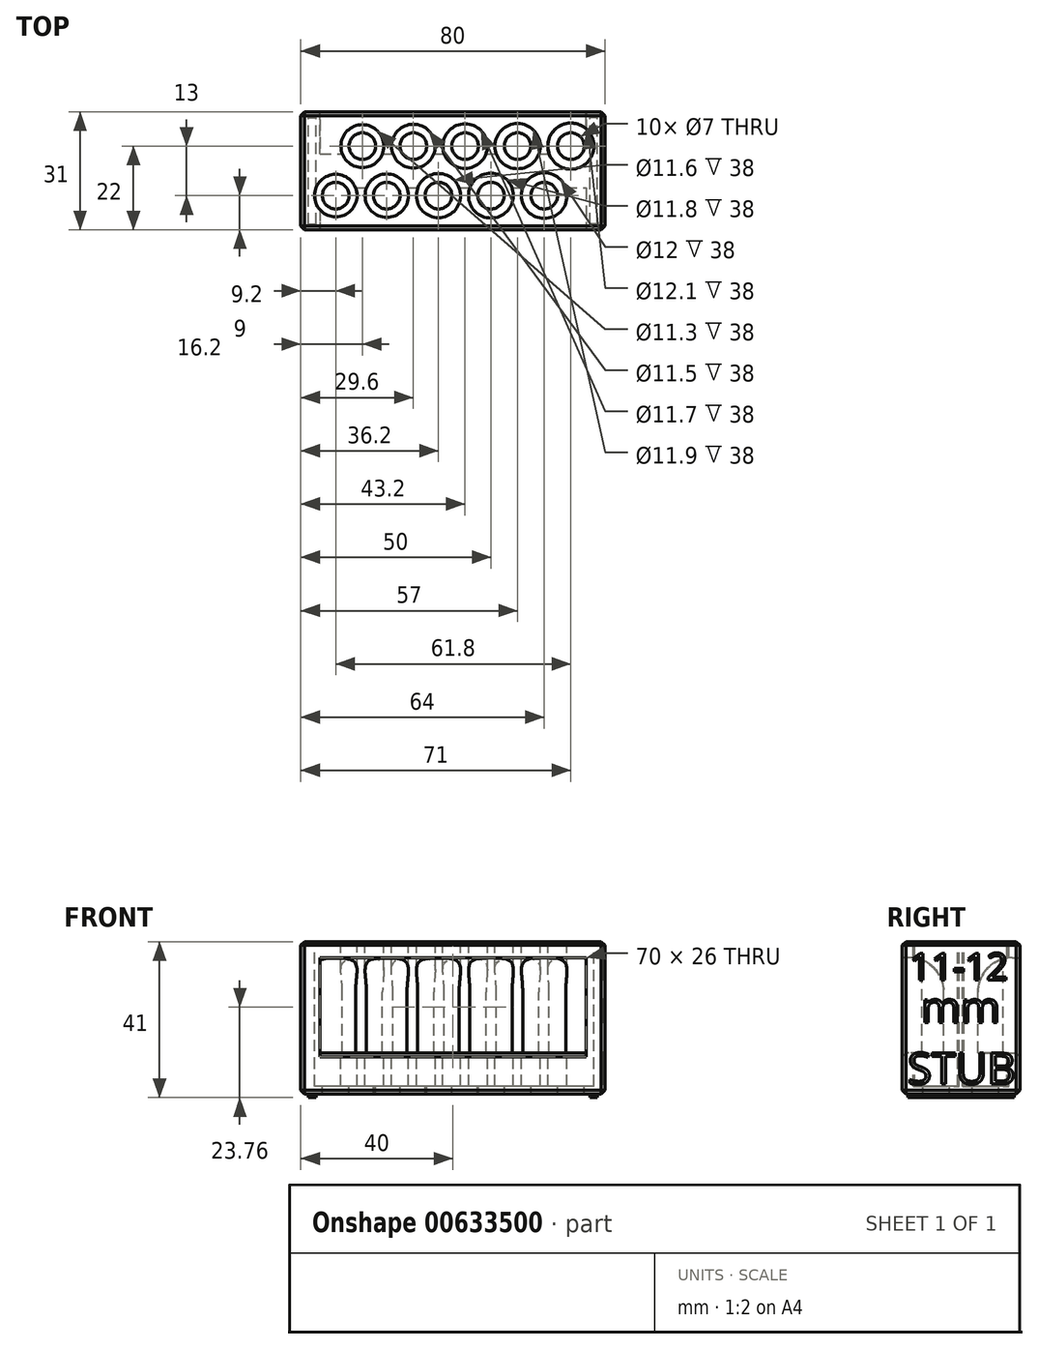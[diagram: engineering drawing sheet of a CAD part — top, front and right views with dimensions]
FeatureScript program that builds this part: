
annotation { "Feature Type Name" : "Feature", "Feature Type Description" : "" }
export const myFeature = defineFeature(function(context is Context, id is Id, definition is map)
    precondition{}
    {
        {
            var Q0;
            Q0=qCreatedBy(makeId("Top.planeOp"),FACE);
            var sketch = newSketch(context, id + "F0", { "sketchPlane" : qUnion([Q0])});
            skCircle(sketch, "E0", {"center": v(0, 0) * mm, "radius": 6.05 * mm});
            skCircle(sketch, "E1.1.0.0", {"center": v(-14, 0) * mm, "radius": 5.95 * mm});
            skCircle(sketch, "E1.2.0.0", {"center": v(-27.8, 0) * mm, "radius": 5.85 * mm});
            skCircle(sketch, "E1.3.0.0", {"center": v(-41.4, 0) * mm, "radius": 5.75 * mm});
            skCircle(sketch, "E1.4.0.0", {"center": v(-54.8, 0) * mm, "radius": 5.65 * mm});
            skLineSegment(sketch, "E1.direction1", {"start": v(0, 0) * mm, "end": v(-14, 0) * mm, "construction": true});
            skLineSegment(sketch, "E2", {"start": v(0, 0) * mm, "end": v(0, -13) * mm, "construction": true});
            skLineSegment(sketch, "E3", {"start": v(0, -13) * mm, "end": v(-90, -13) * mm, "construction": true});
            skCircle(sketch, "E4", {"center": v(-7, -13) * mm, "radius": 6 * mm});
            skCircle(sketch, "E5.1.0.0", {"center": v(-21, -13) * mm, "radius": 5.9 * mm});
            skCircle(sketch, "E5.2.0.0", {"center": v(-34.8, -13) * mm, "radius": 5.8 * mm});
            skCircle(sketch, "E5.3.0.0", {"center": v(-48.4, -13) * mm, "radius": 5.7 * mm});
            skCircle(sketch, "E5.4.0.0", {"center": v(-61.8, -13) * mm, "radius": 5.6 * mm});
            skLineSegment(sketch, "E5.direction1", {"start": v(-7, -13) * mm, "end": v(-21, -13) * mm, "construction": true});
            skSolve(sketch);
        }
        {
            var Q0;
            Q0=qCreatedBy(makeId("Top.planeOp"),FACE);
            var sketch = newSketch(context, id + "F1", { "sketchPlane" : qUnion([Q0])});
            skLineSegment(sketch, "E6.bottom", {"start": v(9, 9) * mm, "end": v(-71, 9) * mm});
            skLineSegment(sketch, "E6.top", {"start": v(9, -22) * mm, "end": v(-71, -22) * mm});
            skLineSegment(sketch, "E6.left", {"start": v(9, 9) * mm, "end": v(9, -22) * mm});
            skLineSegment(sketch, "E6.right", {"start": v(-71, 9) * mm, "end": v(-71, -22) * mm});
            skSolve(sketch);
        }
        {
            var Q0;
            Q0=makeQuery(id+"F1.imprint","IMPRINT",FACE,{"disambiguationData":[TD([[makeQuery(id+"F1.imprint","IMPRINT",EDGE,{"derivedFrom":sQuery(id+"F1.wireOp",EDGE,"E6.bottom")}),1.0]])]});
            extrude(context, id + "F2", {"entities" : qUnion([Q0]), "oppositeDirection" : true, "depth" : 40 * mm, "offsetDistance" : 25 * mm});
        }
        {
            var Q0;
            Q0 = qSketchRegion(id + "F0", true);
            extrude(context, id + "F3", {"entities" : qUnion([Q0]), "operationType" : NewBodyOperationType.REMOVE, "oppositeDirection" : true, "depth" : 38 * mm, "offsetDistance" : 25 * mm});
        }
        {
            var Q0;
            Q0=qCreatedBy(makeId("Top.planeOp"),FACE);
            var sketch = newSketch(context, id + "F4", { "sketchPlane" : qUnion([Q0])});
            skLineSegment(sketch, "E7.direction1", {"start": v(0, 0) * mm, "end": v(-14, 0) * mm, "construction": true});
            skLineSegment(sketch, "E8", {"start": v(0, 0) * mm, "end": v(0, -13) * mm, "construction": true});
            skLineSegment(sketch, "E9", {"start": v(0, -13) * mm, "end": v(-90, -13) * mm, "construction": true});
            skLineSegment(sketch, "E10.direction1", {"start": v(-7, -13) * mm, "end": v(-21, -13) * mm, "construction": true});
            skCircle(sketch, "E11", {"center": v(-54.8, 0) * mm, "radius": 3.5 * mm});
            skCircle(sketch, "E12", {"center": v(-41.4, 0) * mm, "radius": 3.5 * mm});
            skCircle(sketch, "E13", {"center": v(-27.8, 0) * mm, "radius": 3.5 * mm});
            skCircle(sketch, "E14", {"center": v(-14, 0) * mm, "radius": 3.5 * mm});
            skCircle(sketch, "E15", {"center": v(0, 0) * mm, "radius": 3.5 * mm});
            skCircle(sketch, "E16", {"center": v(-61.8, -13) * mm, "radius": 3.5 * mm});
            skCircle(sketch, "E17", {"center": v(-48.4, -13) * mm, "radius": 3.5 * mm});
            skCircle(sketch, "E18", {"center": v(-34.8, -13) * mm, "radius": 3.5 * mm});
            skCircle(sketch, "E19", {"center": v(-21, -13) * mm, "radius": 3.5 * mm});
            skCircle(sketch, "E20", {"center": v(-7, -13) * mm, "radius": 3.5 * mm});
            skSolve(sketch);
        }
        {
            var Q0;
            Q0 = qSketchRegion(id + "F4", true);
            extrude(context, id + "F5", {"entities" : qUnion([Q0]), "operationType" : NewBodyOperationType.REMOVE, "oppositeDirection" : true, "depth" : 50 * mm, "offsetDistance" : 25 * mm});
        }
        {
            var Q0;
            Q0=qCreatedBy(makeId("Right.planeOp"),FACE);
            var sketch = newSketch(context, id + "F6", { "sketchPlane" : qUnion([Q0])});
            skLineSegment(sketch, "E21.bottom", {"start": v(7, -4.24) * mm, "end": v(18, -4.24) * mm});
            skLineSegment(sketch, "E21.top", {"start": v(-2, -29.24) * mm, "end": v(18, -29.24) * mm});
            skLineSegment(sketch, "E21.left", {"start": v(-2, -13.24) * mm, "end": v(-2, -29.24) * mm});
            skLineSegment(sketch, "E21.right", {"start": v(18, -4.24) * mm, "end": v(18, -29.24) * mm});
            skLineSegment(sketch, "E22", {"start": v(0, 0) * mm, "end": v(-6.5, 0) * mm, "construction": true});
            skLineSegment(sketch, "E23", {"start": v(-6.5, 0) * mm, "end": v(-6.5, 18.33) * mm, "construction": true});
            skLineSegment(sketch, "E24.MirrorCS", {"start": v(-11, -13.24) * mm, "end": v(-11, -29.24) * mm});
            skLineSegment(sketch, "E25.MirrorCS", {"start": v(-31, -4.24) * mm, "end": v(-31, -29.24) * mm});
            skLineSegment(sketch, "E26.MirrorCS", {"start": v(-20, -4.24) * mm, "end": v(-31, -4.24) * mm});
            skLineSegment(sketch, "E27.MirrorCS", {"start": v(-11, -29.24) * mm, "end": v(-31, -29.24) * mm});
            skPoint(sketch, "E28.visualSharp", {"position": v(-2, -4.24) * mm});
            skArc(sketch, "E28.filletArc", {"start": v(7, -4.24) * mm, "mid": v(0.64, -6.88) * mm, "end": v(-2, -13.24) * mm});
            skPoint(sketch, "E29.visualSharp", {"position": v(-11, -4.24) * mm});
            skArc(sketch, "E29.filletArc", {"start": v(-11, -13.24) * mm, "mid": v(-13.64, -6.88) * mm, "end": v(-20, -4.24) * mm});
            skSolve(sketch);
        }
        {
            var Q0;
            Q0 = qSketchRegion(id + "F6", true);
            extrude(context, id + "F7", {"entities" : qUnion([Q0]), "operationType" : NewBodyOperationType.REMOVE, "oppositeDirection" : true, "depth" : 66 * mm, "offsetDistance" : 25 * mm, "hasSecondDirection" : true, "secondDirectionOppositeDirection" : false, "secondDirectionDepth" : 4 * mm});
        }
        {
            var Q0;
            Q0=makeQuery(id+"F2.opExtrude","CAP_EDGE",EDGE,{"disambiguationData":[OSD([sQuery(id+"F1.wireOp",EDGE,"E6.right")])],"isStart":true});
            var Q1;
            Q1=makeQuery(id+"F2.opExtrude","CAP_EDGE",EDGE,{"disambiguationData":[OSD([sQuery(id+"F1.wireOp",EDGE,"E6.bottom")])],"isStart":true});
            var Q2;
            Q2=makeQuery(id+"F2.opExtrude","CAP_EDGE",EDGE,{"disambiguationData":[OSD([sQuery(id+"F1.wireOp",EDGE,"E6.top")])],"isStart":true});
            var Q3;
            Q3=makeQuery(id+"F2.opExtrude","CAP_EDGE",EDGE,{"disambiguationData":[OSD([sQuery(id+"F1.wireOp",EDGE,"E6.left")])],"isStart":true});
            var Q4;
            Q4=makeQuery(id+"F2.opExtrude","SWEPT_EDGE",EDGE,{"disambiguationData":[OSD([sQuery(id+"F1.wireOp",EDGE,"E6.top"),sQuery(id+"F1.wireOp",EDGE,"E6.right")])]});
            var Q5;
            Q5=makeQuery(id+"F2.opExtrude","CAP_EDGE",EDGE,{"disambiguationData":[OSD([sQuery(id+"F1.wireOp",EDGE,"E6.right")])],"isStart":false});
            var Q6;
            Q6=makeQuery(id+"F2.opExtrude","SWEPT_EDGE",EDGE,{"disambiguationData":[OSD([sQuery(id+"F1.wireOp",EDGE,"E6.bottom"),sQuery(id+"F1.wireOp",EDGE,"E6.right")])]});
            var Q7;
            Q7=makeQuery(id+"F2.opExtrude","SWEPT_FACE",FACE,{"disambiguationData":[OSD([sQuery(id+"F1.wireOp",EDGE,"E6.left")])]});
            var Q8;
            Q8=makeQuery(id+"F2.opExtrude","CAP_EDGE",EDGE,{"disambiguationData":[OSD([sQuery(id+"F1.wireOp",EDGE,"E6.top")])],"isStart":false});
            var Q9;
            Q9=makeQuery(id+"F2.opExtrude","CAP_EDGE",EDGE,{"disambiguationData":[OSD([sQuery(id+"F1.wireOp",EDGE,"E6.bottom")])],"isStart":false});
            var Q10;
            Q10=makeQuery(id+"F7.boolean.opBoolean","INTERSECT",EDGE,{"derivedFrom":[makeQuery(id+"F2.opExtrude","SWEPT_FACE",FACE,{"disambiguationData":[OSD([sQuery(id+"F1.wireOp",EDGE,"E6.bottom")])]}),makeQuery(id+"F7.opExtrude","SWEPT_FACE",FACE,{"disambiguationData":[OSD([sQuery(id+"F6.wireOp",EDGE,"E21.top")])]})]});
            var Q11;
            Q11=makeQuery(id+"F7.boolean.opBoolean","INTERSECT",EDGE,{"derivedFrom":[makeQuery(id+"F2.opExtrude","SWEPT_FACE",FACE,{"disambiguationData":[OSD([sQuery(id+"F1.wireOp",EDGE,"E6.top")])]}),makeQuery(id+"F7.opExtrude","SWEPT_FACE",FACE,{"disambiguationData":[OSD([sQuery(id+"F6.wireOp",EDGE,"E27.MirrorCS")])]})]});
            chamfer(context, id + "F8", {"entities" : qUnion([Q0, Q1, Q2, Q3, Q4, Q5, Q6, Q7, Q8, Q9, Q10, Q11]), "width" : 1 * mm, "tangentPropagation" : true});
        }
        {
            var Q0;
            Q0=qCreatedBy(makeId("Right.planeOp"),FACE);
            var sketch = newSketch(context, id + "F9", { "sketchPlane" : qUnion([Q0])});
            skText(sketch, "E30", { "text": "11-12\n", "fontName": "NotoSans-Regular.ttf"});
            skText(sketch, "E31", { "text": "mm", "fontName": "OpenSans-Regular.ttf"});
            skText(sketch, "E32", { "text": "STUB", "fontName": "OpenSans-Regular.ttf"});
            const initialGuessF9  = {"E30": [-0.02, -0.01014, 1, 0, 0.00714], "E31": [-0.017, -0.0213, 1, 0, 0.00806], "E32": [-0.0205, -0.03743, 1, 0, 0.00824]};
            skSetInitialGuess(sketch, initialGuessF9);
            skSolve(sketch);
        }
        {
            var Q0;
            Q0 = qSketchRegion(id + "F9", true);
            extrude(context, id + "F10", {"entities" : qUnion([Q0]), "operationType" : NewBodyOperationType.REMOVE, "depth" : 25 * mm, "offsetDistance" : 25 * mm, "hasSecondDirection" : true, "secondDirectionOppositeDirection" : false, "secondDirectionDepth" : 8.5 * mm});
        }
        {
            var Q0;
            Q0=qCreatedBy(makeId("Top.planeOp"),FACE);
            var sketch = newSketch(context, id + "F11", { "sketchPlane" : qUnion([Q0])});
            skLineSegment(sketch, "E33.bottom", {"start": v(7, -20.5) * mm, "end": v(5, -20.5) * mm});
            skLineSegment(sketch, "E33.top", {"start": v(7, 7.5) * mm, "end": v(5, 7.5) * mm});
            skLineSegment(sketch, "E33.left", {"start": v(7, -20.5) * mm, "end": v(7, 7.5) * mm});
            skLineSegment(sketch, "E33.right", {"start": v(5, -20.5) * mm, "end": v(5, 7.5) * mm});
            skLineSegment(sketch, "E34", {"start": v(0, 0) * mm, "end": v(-31, 0) * mm, "construction": true});
            skLineSegment(sketch, "E35", {"start": v(-31, 0) * mm, "end": v(-31, -86.92) * mm, "construction": true});
            skLineSegment(sketch, "E36.MirrorCS", {"start": v(-67, -20.5) * mm, "end": v(-67, 7.5) * mm});
            skLineSegment(sketch, "E37.MirrorCS", {"start": v(-69, -20.5) * mm, "end": v(-69, 7.5) * mm});
            skLineSegment(sketch, "E38.MirrorCS", {"start": v(-69, 7.5) * mm, "end": v(-67, 7.5) * mm});
            skLineSegment(sketch, "E39.MirrorCS", {"start": v(-69, -20.5) * mm, "end": v(-67, -20.5) * mm});
            skSolve(sketch);
        }
        {
            var Q0;
            Q0 = qSketchRegion(id + "F11", true);
            extrude(context, id + "F12", {"entities" : qUnion([Q0]), "operationType" : NewBodyOperationType.ADD, "oppositeDirection" : true, "depth" : 41 * mm, "offsetDistance" : 25 * mm, "hasSecondDirection" : true, "secondDirectionOppositeDirection" : true, "secondDirectionDepth" : 39 * mm});
        }
    });
